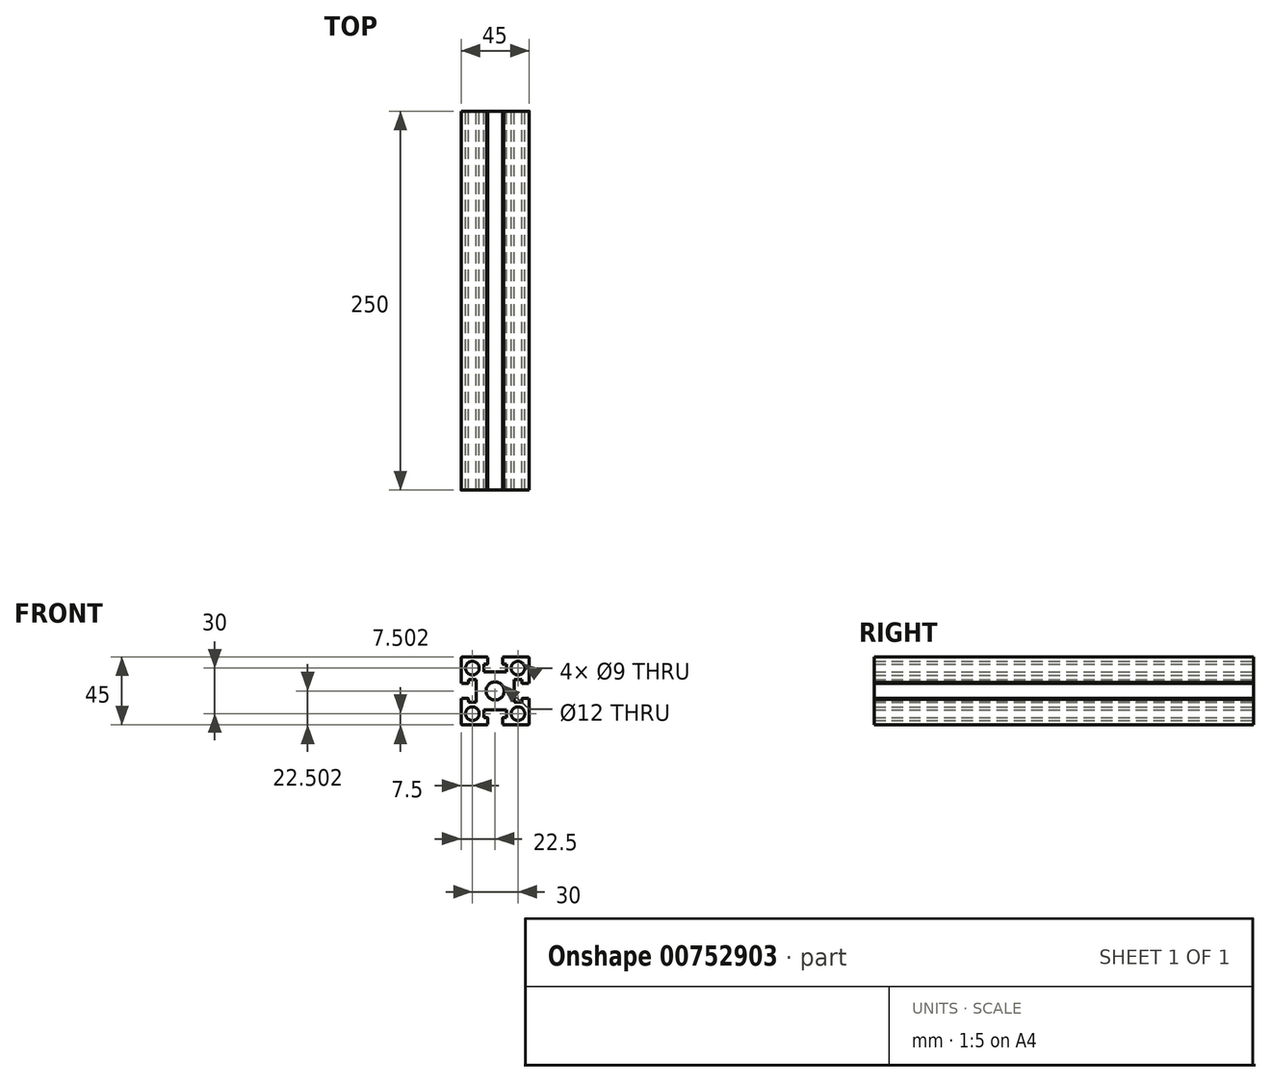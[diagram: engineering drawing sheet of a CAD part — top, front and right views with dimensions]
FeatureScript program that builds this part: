
annotation { "Feature Type Name" : "Feature", "Feature Type Description" : "" }
export const myFeature = defineFeature(function(context is Context, id is Id, definition is map)
    precondition{}
    {
        {
            var Q0;
            Q0=qCreatedBy(makeId("Front.planeOp"),FACE);
            var sketch = newSketch(context, id + "F0", { "sketchPlane" : qUnion([Q0])});
            skLineSegment(sketch, "E0.left", {"start": v(21.97, -23.6) * mm, "end": v(21.97, -6.1) * mm});
            skLineSegment(sketch, "E0.right", {"start": v(-23.03, -23.6) * mm, "end": v(-23.03, -6.1) * mm});
            skPoint(sketch, "E0.middle", {"position": v(-0.53, -1.1) * mm});
            skCircle(sketch, "E1", {"center": v(-0.53, -1.1) * mm, "radius": 6 * mm});
            skLineSegment(sketch, "E2.bottom", {"start": v(-23.03, 3.9) * mm, "end": v(-18.03, 3.9) * mm});
            skLineSegment(sketch, "E2.top", {"start": v(-23.03, -6.1) * mm, "end": v(-18.03, -6.1) * mm});
            skLineSegment(sketch, "E3", {"start": v(-18.03, 3.9) * mm, "end": v(-18.03, 6.4) * mm});
            skLineSegment(sketch, "E4", {"start": v(-18.03, 6.4) * mm, "end": v(-13.03, 6.4) * mm});
            skLineSegment(sketch, "E5", {"start": v(-13.03, 6.4) * mm, "end": v(-13.03, -8.6) * mm});
            skLineSegment(sketch, "E6", {"start": v(-18.03, -6.1) * mm, "end": v(-18.03, -8.6) * mm});
            skLineSegment(sketch, "E7", {"start": v(-18.03, -8.6) * mm, "end": v(-13.03, -8.6) * mm});
            skLineSegment(sketch, "E8.trimOffspring", {"start": v(-23.03, 3.9) * mm, "end": v(-23.03, 21.4) * mm});
            skLineSegment(sketch, "E9.MirrorCS", {"start": v(21.97, -6.1) * mm, "end": v(16.97, -6.1) * mm});
            skLineSegment(sketch, "E10.MirrorCS", {"start": v(16.97, -8.6) * mm, "end": v(11.97, -8.6) * mm});
            skLineSegment(sketch, "E11.MirrorCS", {"start": v(11.97, 6.4) * mm, "end": v(11.97, -8.6) * mm});
            skLineSegment(sketch, "E12.MirrorCS", {"start": v(16.97, 6.4) * mm, "end": v(11.97, 6.4) * mm});
            skLineSegment(sketch, "E13.MirrorCS", {"start": v(21.97, 3.9) * mm, "end": v(16.97, 3.9) * mm});
            skLineSegment(sketch, "E14", {"start": v(16.97, 6.4) * mm, "end": v(16.97, 3.9) * mm});
            skLineSegment(sketch, "E15", {"start": v(16.97, -6.1) * mm, "end": v(16.97, -8.6) * mm});
            skLineSegment(sketch, "E16.trimOffspring", {"start": v(21.97, 3.9) * mm, "end": v(21.97, 21.4) * mm});
            skPoint(sketch, "E17", {"position": v(14.47, -16.1) * mm});
            skPoint(sketch, "E18", {"position": v(14.47, 13.9) * mm});
            skPoint(sketch, "E19", {"position": v(-15.53, 13.9) * mm});
            skPoint(sketch, "E20", {"position": v(-15.53, -16.1) * mm});
            skCircle(sketch, "E21", {"center": v(14.47, -16.1) * mm, "radius": 4.5 * mm});
            skCircle(sketch, "E22", {"center": v(-15.53, -16.1) * mm, "radius": 4.5 * mm});
            skCircle(sketch, "E23", {"center": v(-15.53, 13.9) * mm, "radius": 4.5 * mm});
            skCircle(sketch, "E24", {"center": v(14.47, 13.9) * mm, "radius": 4.5 * mm});
            skLineSegment(sketch, "E25", {"start": v(-23.03, 21.4) * mm, "end": v(-5.53, 21.4) * mm});
            skLineSegment(sketch, "E26", {"start": v(-23.03, -23.6) * mm, "end": v(-5.53, -23.6) * mm});
            skLineSegment(sketch, "E27.left", {"start": v(-5.53, 21.4) * mm, "end": v(-5.53, 16.4) * mm});
            skLineSegment(sketch, "E27.right", {"start": v(4.47, 21.4) * mm, "end": v(4.47, 16.4) * mm});
            skLineSegment(sketch, "E28.bottom", {"start": v(-8.03, 16.4) * mm, "end": v(-5.53, 16.4) * mm});
            skLineSegment(sketch, "E28.top", {"start": v(-8.03, 11.4) * mm, "end": v(6.97, 11.4) * mm});
            skLineSegment(sketch, "E28.left", {"start": v(-8.03, 16.4) * mm, "end": v(-8.03, 11.4) * mm});
            skLineSegment(sketch, "E28.right", {"start": v(6.97, 16.4) * mm, "end": v(6.97, 11.4) * mm});
            skLineSegment(sketch, "E29.trimOffspring", {"start": v(4.47, 21.4) * mm, "end": v(21.97, 21.4) * mm});
            skLineSegment(sketch, "E30.trimOffspring", {"start": v(4.47, 16.4) * mm, "end": v(6.97, 16.4) * mm});
            skLineSegment(sketch, "E31.left", {"start": v(-5.53, -23.6) * mm, "end": v(-5.53, -18.6) * mm});
            skLineSegment(sketch, "E31.right", {"start": v(4.47, -23.6) * mm, "end": v(4.47, -18.6) * mm});
            skLineSegment(sketch, "E32.bottom", {"start": v(-8.03, -13.6) * mm, "end": v(6.97, -13.6) * mm});
            skLineSegment(sketch, "E32.top", {"start": v(-8.03, -18.6) * mm, "end": v(-5.53, -18.6) * mm});
            skLineSegment(sketch, "E32.left", {"start": v(-8.03, -13.6) * mm, "end": v(-8.03, -18.6) * mm});
            skLineSegment(sketch, "E32.right", {"start": v(6.97, -13.6) * mm, "end": v(6.97, -18.6) * mm});
            skLineSegment(sketch, "E33.bottom", {"start": v(6.97, -13.6) * mm, "end": v(6.97, -13.6) * mm});
            skLineSegment(sketch, "E33.top", {"start": v(6.97, -18.6) * mm, "end": v(6.97, -18.6) * mm});
            skLineSegment(sketch, "E34.trimOffspring", {"start": v(4.47, -18.6) * mm, "end": v(6.97, -18.6) * mm});
            skLineSegment(sketch, "E35.trimOffspring", {"start": v(4.47, -23.6) * mm, "end": v(21.97, -23.6) * mm});
            skSolve(sketch);
        }
        {
            var Q0;
            Q0=makeQuery(id+"F0.imprint","IMPRINT",FACE,{"disambiguationData":[TD([[makeQuery(id+"F0.imprint","IMPRINT",EDGE,{"derivedFrom":sQuery(id+"F0.wireOp",EDGE,"E0.left")}),1.0]])]});
            extrude(context, id + "F1", {"entities" : qUnion([Q0]), "depth" : 250 * mm, "offsetDistance" : 25 * mm});
        }
        {
            var Q0;
            Q0=makeQuery(id+"F1.opExtrude","SWEPT_EDGE",EDGE,{"disambiguationData":[OSD([sQuery(id+"F0.wireOp",EDGE,"E16.trimOffspring"),sQuery(id+"F0.wireOp",EDGE,"E29.trimOffspring")])]});
            var Q1;
            Q1=makeQuery(id+"F1.opExtrude","SWEPT_EDGE",EDGE,{"disambiguationData":[OSD([sQuery(id+"F0.wireOp",EDGE,"E0.left"),sQuery(id+"F0.wireOp",EDGE,"E35.trimOffspring")])]});
            var Q2;
            Q2=makeQuery(id+"F1.opExtrude","SWEPT_EDGE",EDGE,{"disambiguationData":[OSD([sQuery(id+"F0.wireOp",EDGE,"E0.right"),sQuery(id+"F0.wireOp",EDGE,"E26")])]});
            var Q3;
            Q3=makeQuery(id+"F1.opExtrude","SWEPT_EDGE",EDGE,{"disambiguationData":[OSD([sQuery(id+"F0.wireOp",EDGE,"E8.trimOffspring"),sQuery(id+"F0.wireOp",EDGE,"E25")])]});
            fillet(context, id + "F2", {"entities" : qUnion([Q0, Q1, Q2, Q3]), "radius" : 1 * mm, "tangentPropagation" : true, "allowEdgeOverflow" : false});
        }
        {
            var Q0;
            Q0=makeQuery(id+"F1.opExtrude","SWEPT_EDGE",EDGE,{"disambiguationData":[OSD([sQuery(id+"F0.wireOp",EDGE,"E2.top"),sQuery(id+"F0.wireOp",EDGE,"E6")])]});
            var Q1;
            Q1=makeQuery(id+"F1.opExtrude","SWEPT_EDGE",EDGE,{"disambiguationData":[OSD([sQuery(id+"F0.wireOp",EDGE,"E2.bottom"),sQuery(id+"F0.wireOp",EDGE,"E3")])]});
            var Q2;
            Q2=makeQuery(id+"F1.opExtrude","SWEPT_EDGE",EDGE,{"disambiguationData":[OSD([sQuery(id+"F0.wireOp",EDGE,"E31.left"),sQuery(id+"F0.wireOp",EDGE,"E32.top")])]});
            var Q3;
            Q3=makeQuery(id+"F1.opExtrude","SWEPT_EDGE",EDGE,{"disambiguationData":[OSD([sQuery(id+"F0.wireOp",EDGE,"E31.right"),sQuery(id+"F0.wireOp",EDGE,"E34.trimOffspring")])]});
            var Q4;
            Q4=makeQuery(id+"F1.opExtrude","SWEPT_EDGE",EDGE,{"disambiguationData":[OSD([sQuery(id+"F0.wireOp",EDGE,"E9.MirrorCS"),sQuery(id+"F0.wireOp",EDGE,"E15")])]});
            var Q5;
            Q5=makeQuery(id+"F1.opExtrude","SWEPT_EDGE",EDGE,{"disambiguationData":[OSD([sQuery(id+"F0.wireOp",EDGE,"E27.left"),sQuery(id+"F0.wireOp",EDGE,"E28.bottom")])]});
            var Q6;
            Q6=makeQuery(id+"F1.opExtrude","SWEPT_EDGE",EDGE,{"disambiguationData":[OSD([sQuery(id+"F0.wireOp",EDGE,"E27.right"),sQuery(id+"F0.wireOp",EDGE,"E30.trimOffspring")])]});
            var Q7;
            Q7=makeQuery(id+"F1.opExtrude","SWEPT_EDGE",EDGE,{"disambiguationData":[OSD([sQuery(id+"F0.wireOp",EDGE,"E13.MirrorCS"),sQuery(id+"F0.wireOp",EDGE,"E14")])]});
            fillet(context, id + "F3", {"entities" : qUnion([Q0, Q1, Q2, Q3, Q4, Q5, Q6, Q7]), "radius" : .5 * mm, "tangentPropagation" : true, "allowEdgeOverflow" : false});
        }
        {
            var Q0;
            Q0=makeQuery(id+"F1.opExtrude","SWEPT_EDGE",EDGE,{"disambiguationData":[OSD([sQuery(id+"F0.wireOp",EDGE,"E0.left"),sQuery(id+"F0.wireOp",EDGE,"E9.MirrorCS")])]});
            var Q1;
            Q1=makeQuery(id+"F1.opExtrude","SWEPT_EDGE",EDGE,{"disambiguationData":[OSD([sQuery(id+"F0.wireOp",EDGE,"E13.MirrorCS"),sQuery(id+"F0.wireOp",EDGE,"E16.trimOffspring")])]});
            var Q2;
            Q2=makeQuery(id+"F1.opExtrude","SWEPT_EDGE",EDGE,{"disambiguationData":[OSD([sQuery(id+"F0.wireOp",EDGE,"E27.right"),sQuery(id+"F0.wireOp",EDGE,"E29.trimOffspring")])]});
            var Q3;
            Q3=makeQuery(id+"F1.opExtrude","SWEPT_EDGE",EDGE,{"disambiguationData":[OSD([sQuery(id+"F0.wireOp",EDGE,"E25"),sQuery(id+"F0.wireOp",EDGE,"E27.left")])]});
            var Q4;
            Q4=makeQuery(id+"F1.opExtrude","SWEPT_EDGE",EDGE,{"disambiguationData":[OSD([sQuery(id+"F0.wireOp",EDGE,"E2.bottom"),sQuery(id+"F0.wireOp",EDGE,"E8.trimOffspring")])]});
            var Q5;
            Q5=makeQuery(id+"F1.opExtrude","SWEPT_EDGE",EDGE,{"disambiguationData":[OSD([sQuery(id+"F0.wireOp",EDGE,"E0.right"),sQuery(id+"F0.wireOp",EDGE,"E2.top")])]});
            var Q6;
            Q6=makeQuery(id+"F1.opExtrude","SWEPT_EDGE",EDGE,{"disambiguationData":[OSD([sQuery(id+"F0.wireOp",EDGE,"E31.right"),sQuery(id+"F0.wireOp",EDGE,"E35.trimOffspring")])]});
            var Q7;
            Q7=makeQuery(id+"F1.opExtrude","SWEPT_EDGE",EDGE,{"disambiguationData":[OSD([sQuery(id+"F0.wireOp",EDGE,"E26"),sQuery(id+"F0.wireOp",EDGE,"E31.left")])]});
            chamfer(context, id + "F4", {"entities" : qUnion([Q0, Q1, Q2, Q3, Q4, Q5, Q6, Q7]), "width" : .5 * mm, "tangentPropagation" : true});
        }
    });
